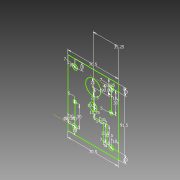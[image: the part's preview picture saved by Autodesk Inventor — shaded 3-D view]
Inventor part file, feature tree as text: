
AUTODESK INVENTOR PART (.ipt)
format: ipt  version: 2015 (Build 190159000, 159)  size: 94,720 bytes
history: native  units: mm
features: sketch x1
ambient origin geometry x8: Origin, YZ Plane, XZ Plane, XY Plane, X Axis, Y Axis, Z Axis, Center Point
feature tree (1):
  sketch  "Sketch1"  dims[d0=21.0mm d1=23.5mm d2=10.5mm d3=11.75mm d4=14.0mm d5=23.5mm d6=5.0mm d7=23.5mm d8=10.0mm d9=70.5mm d11=35.25mm d12=91.5mm d13=70.5mm d14=21.625mm d15=10.0mm d16=10.0mm d18=10.0mm d19=10.0mm d20=10.0mm d21=10.0mm d22=10.0mm d23=10.0mm d30=7.0mm d31=7.0mm d32=7.0mm d33=7.0mm d34=30.0mm d35=90.0deg d36=30.0mm d37=90.0deg d38=5.0mm d39=5.0mm]
